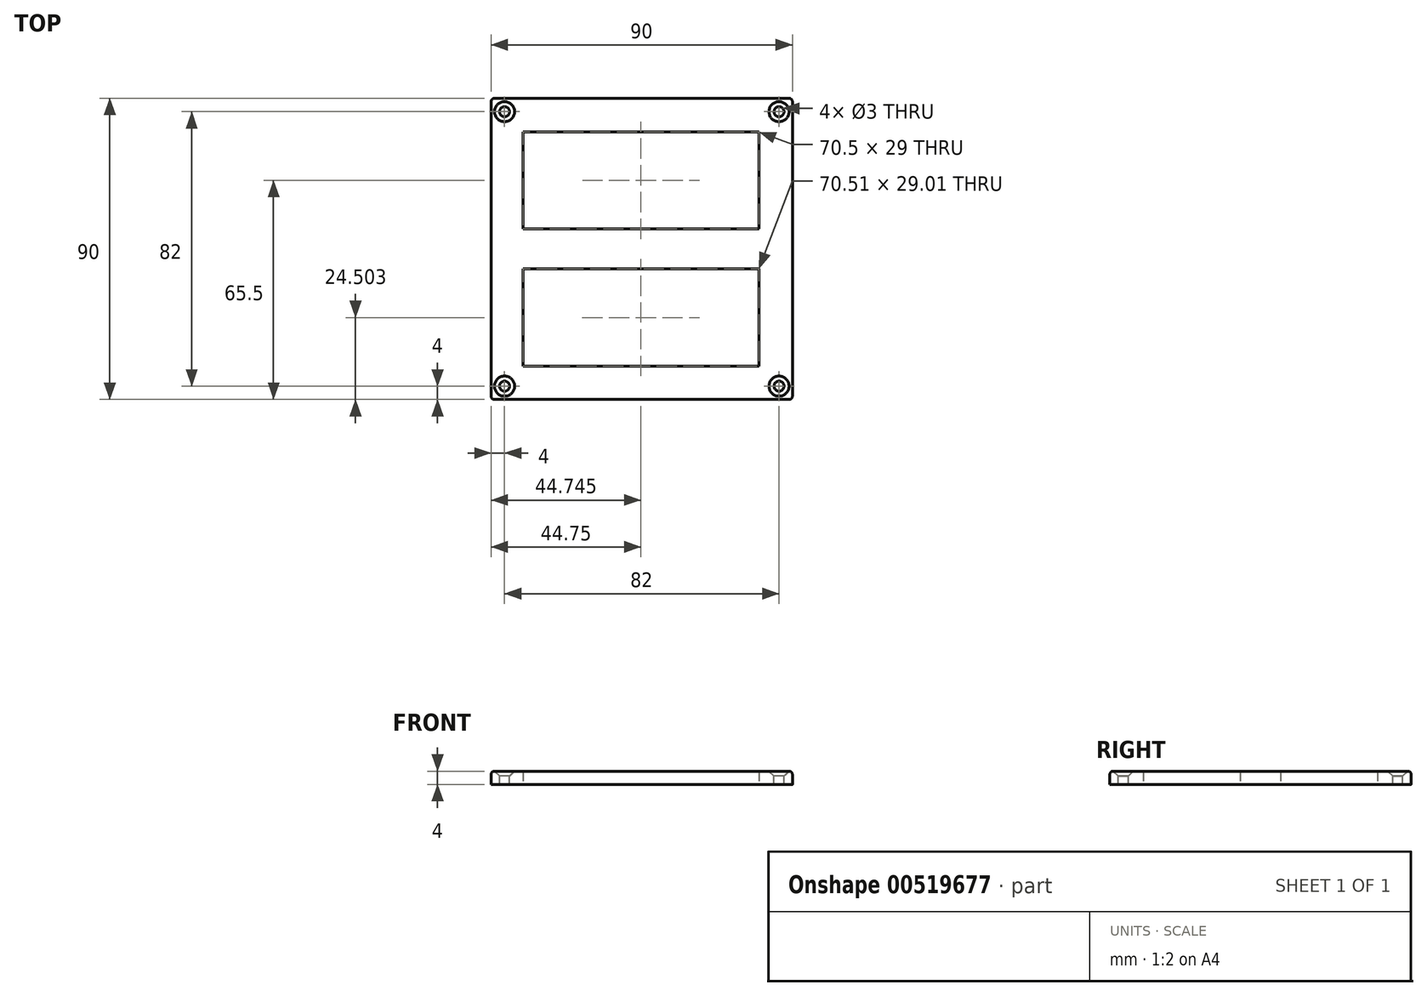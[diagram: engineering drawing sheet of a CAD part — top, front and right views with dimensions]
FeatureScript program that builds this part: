
annotation { "Feature Type Name" : "Feature", "Feature Type Description" : "" }
export const myFeature = defineFeature(function(context is Context, id is Id, definition is map)
    precondition{}
    {
        {
            var Q0;
            Q0=qCreatedBy(makeId("Top.planeOp"),FACE);
            var sketch = newSketch(context, id + "F0", { "sketchPlane" : qUnion([Q0])});
            skLineSegment(sketch, "E0.bottom", {"start": v(-45, 45) * mm, "end": v(45, 45) * mm});
            skLineSegment(sketch, "E0.top", {"start": v(-45, -45) * mm, "end": v(45, -45) * mm});
            skLineSegment(sketch, "E0.left", {"start": v(-45, 45) * mm, "end": v(-45, -45) * mm});
            skLineSegment(sketch, "E0.right", {"start": v(45, 45) * mm, "end": v(45, -45) * mm});
            skLineSegment(sketch, "E1.bottom", {"start": v(-35.5, 35) * mm, "end": v(35, 35) * mm});
            skLineSegment(sketch, "E1.top", {"start": v(-35.5, 6) * mm, "end": v(35, 6) * mm});
            skLineSegment(sketch, "E1.left", {"start": v(-35.5, 35) * mm, "end": v(-35.5, 6) * mm});
            skLineSegment(sketch, "E1.right", {"start": v(35, 35) * mm, "end": v(35, 6) * mm});
            skLineSegment(sketch, "E2.bottom", {"start": v(-35.51, -6) * mm, "end": v(35, -6) * mm});
            skLineSegment(sketch, "E2.top", {"start": v(-35.51, -35) * mm, "end": v(35, -35) * mm});
            skLineSegment(sketch, "E2.left", {"start": v(-35.51, -6) * mm, "end": v(-35.51, -35) * mm});
            skLineSegment(sketch, "E2.right", {"start": v(35, -6) * mm, "end": v(35, -35) * mm});
            skSolve(sketch);
        }
        {
            var Q0;
            Q0=makeQuery(id+"F0.imprint","IMPRINT",FACE,{"disambiguationData":[TD([[makeQuery(id+"F0.imprint","IMPRINT",EDGE,{"derivedFrom":sQuery(id+"F0.wireOp",EDGE,"E0.bottom")}),-1.0]])]});
            extrude(context, id + "F1", {"entities" : qUnion([Q0]), "depth" : 4 * mm, "offsetDistance" : 25.4 * mm});
        }
        {
            var Q0;
            Q0=makeQuery(id+"F1.opExtrude","CAP_FACE",FACE,{"disambiguationData":[OSD([sQuery(id+"F0.wireOp",EDGE,"E0.bottom"),sQuery(id+"F0.wireOp",EDGE,"E0.top"),sQuery(id+"F0.wireOp",EDGE,"E0.left"),sQuery(id+"F0.wireOp",EDGE,"E0.right"),sQuery(id+"F0.wireOp",EDGE,"E1.bottom"),sQuery(id+"F0.wireOp",EDGE,"E1.top"),sQuery(id+"F0.wireOp",EDGE,"E1.left"),sQuery(id+"F0.wireOp",EDGE,"E1.right"),sQuery(id+"F0.wireOp",EDGE,"E2.bottom"),sQuery(id+"F0.wireOp",EDGE,"E2.top"),sQuery(id+"F0.wireOp",EDGE,"E2.left"),sQuery(id+"F0.wireOp",EDGE,"E2.right")])],"isStart":false});
            var sketch = newSketch(context, id + "F2", { "sketchPlane" : qUnion([Q0])});
            skPoint(sketch, "E3", {"position": v(-41, 41) * mm});
            skPoint(sketch, "E4", {"position": v(41, 41) * mm});
            skPoint(sketch, "E5", {"position": v(41, -41) * mm});
            skPoint(sketch, "E6", {"position": v(-41, -41) * mm});
            skSolve(sketch);
        }
        {
            var Q0;
            Q0=sQuery(id+"F2.wireOp",VERTEX,"E3");
            var Q1;
            Q1=sQuery(id+"F2.wireOp",VERTEX,"E4");
            var Q2;
            Q2=sQuery(id+"F2.wireOp",VERTEX,"E5");
            var Q3;
            Q3=sQuery(id+"F2.wireOp",VERTEX,"E6");
            var Q4;
            Q4=makeQuery(id+"F1.opExtrude","SWEPT_BODY",BODY,{"disambiguationData":[OSD([sQuery(id+"F0.wireOp",EDGE,"E0.bottom"),sQuery(id+"F0.wireOp",EDGE,"E0.top"),sQuery(id+"F0.wireOp",EDGE,"E0.left"),sQuery(id+"F0.wireOp",EDGE,"E0.right"),sQuery(id+"F0.wireOp",EDGE,"E1.bottom"),sQuery(id+"F0.wireOp",EDGE,"E1.top"),sQuery(id+"F0.wireOp",EDGE,"E1.left"),sQuery(id+"F0.wireOp",EDGE,"E1.right"),sQuery(id+"F0.wireOp",EDGE,"E2.bottom"),sQuery(id+"F0.wireOp",EDGE,"E2.top"),sQuery(id+"F0.wireOp",EDGE,"E2.left"),sQuery(id+"F0.wireOp",EDGE,"E2.right")])]});
            hole(context, id + "F3", {"style" : HoleStyle.C_SINK, "endStyle" : HoleEndStyle.THROUGH, "holeDiameter" : 3 * mm, "cSinkDiameter" : 6 * mm, "cSinkAngle" : 90 * degree, "isTappedThrough" : true, "tappedDepth" : 12.7 * mm, "tapClearance" : 3, "locations" : qUnion([Q0, Q1, Q2, Q3]), "scope" : qUnion([Q4])});
        }
        {
            var Q0;
            Q0=makeQuery(id+"F1.opExtrude","CAP_EDGE",EDGE,{"disambiguationData":[OSD([sQuery(id+"F0.wireOp",EDGE,"E0.bottom")])],"isStart":false});
            var Q1;
            Q1=makeQuery(id+"F1.opExtrude","CAP_EDGE",EDGE,{"disambiguationData":[OSD([sQuery(id+"F0.wireOp",EDGE,"E0.left")])],"isStart":false});
            var Q2;
            Q2=makeQuery(id+"F1.opExtrude","CAP_EDGE",EDGE,{"disambiguationData":[OSD([sQuery(id+"F0.wireOp",EDGE,"E0.top")])],"isStart":false});
            var Q3;
            Q3=makeQuery(id+"F1.opExtrude","CAP_EDGE",EDGE,{"disambiguationData":[OSD([sQuery(id+"F0.wireOp",EDGE,"E0.right")])],"isStart":false});
            var Q4;
            Q4=makeQuery(id+"F1.opExtrude","SWEPT_EDGE",EDGE,{"disambiguationData":[OSD([sQuery(id+"F0.wireOp",EDGE,"E0.top"),sQuery(id+"F0.wireOp",EDGE,"E0.right")])]});
            var Q5;
            Q5=makeQuery(id+"F1.opExtrude","SWEPT_EDGE",EDGE,{"disambiguationData":[OSD([sQuery(id+"F0.wireOp",EDGE,"E0.bottom"),sQuery(id+"F0.wireOp",EDGE,"E0.right")])]});
            var Q6;
            Q6=makeQuery(id+"F1.opExtrude","SWEPT_EDGE",EDGE,{"disambiguationData":[OSD([sQuery(id+"F0.wireOp",EDGE,"E0.bottom"),sQuery(id+"F0.wireOp",EDGE,"E0.left")])]});
            var Q7;
            Q7=makeQuery(id+"F1.opExtrude","SWEPT_EDGE",EDGE,{"disambiguationData":[OSD([sQuery(id+"F0.wireOp",EDGE,"E0.top"),sQuery(id+"F0.wireOp",EDGE,"E0.left")])]});
            fillet(context, id + "F4", {"entities" : qUnion([Q0, Q1, Q2, Q3, Q4, Q5, Q6, Q7]), "radius" : 1 * mm, "tangentPropagation" : true, "allowEdgeOverflow" : false});
        }
    });
